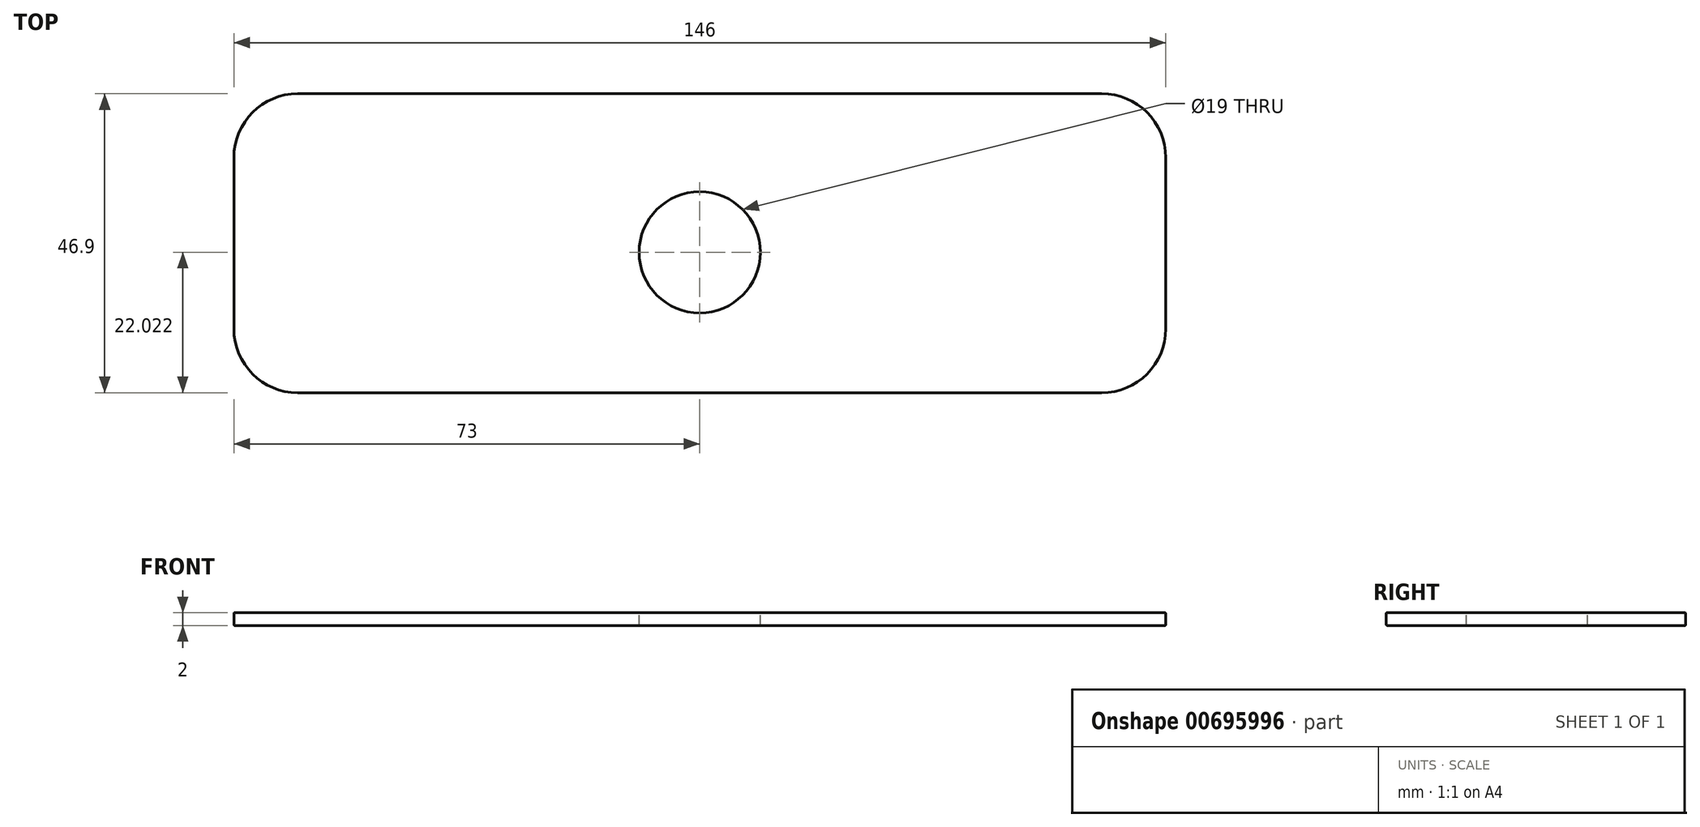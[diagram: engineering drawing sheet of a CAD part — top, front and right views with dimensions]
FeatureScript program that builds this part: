
annotation { "Feature Type Name" : "Feature", "Feature Type Description" : "" }
export const myFeature = defineFeature(function(context is Context, id is Id, definition is map)
    precondition{}
    {
        {
            var Q0;
            Q0=qCreatedBy(makeId("Top.planeOp"),FACE);
            var sketch = newSketch(context, id + "F0", { "sketchPlane" : qUnion([Q0])});
            skLineSegment(sketch, "E0.bottom", {"start": v(73, 23.45) * mm, "end": v(-73, 23.45) * mm});
            skLineSegment(sketch, "E0.top", {"start": v(73, -23.45) * mm, "end": v(-73, -23.45) * mm});
            skLineSegment(sketch, "E0.left", {"start": v(73, 23.45) * mm, "end": v(73, -23.45) * mm});
            skLineSegment(sketch, "E0.right", {"start": v(-73, 23.45) * mm, "end": v(-73, -23.45) * mm});
            skPoint(sketch, "E0.middle", {"position": v(0, 0) * mm});
            skSolve(sketch);
        }
        {
            var Q0;
            Q0=makeQuery(id+"F0.imprint","IMPRINT",FACE,{"disambiguationData":[TD([[makeQuery(id+"F0.imprint","IMPRINT",EDGE,{"derivedFrom":sQuery(id+"F0.wireOp",EDGE,"E0.bottom")}),1.0]])]});
            extrude(context, id + "F1", {"entities" : qUnion([Q0]), "depth" : 2 * mm, "offsetDistance" : 25 * mm});
        }
        {
            var Q0;
            Q0=makeQuery(id+"F1.opExtrude","SWEPT_EDGE",EDGE,{"disambiguationData":[OSD([sQuery(id+"F0.wireOp",EDGE,"E0.top"),sQuery(id+"F0.wireOp",EDGE,"E0.left")])]});
            var Q1;
            Q1=makeQuery(id+"F1.opExtrude","SWEPT_EDGE",EDGE,{"disambiguationData":[OSD([sQuery(id+"F0.wireOp",EDGE,"E0.bottom"),sQuery(id+"F0.wireOp",EDGE,"E0.left")])]});
            var Q2;
            Q2=makeQuery(id+"F1.opExtrude","SWEPT_EDGE",EDGE,{"disambiguationData":[OSD([sQuery(id+"F0.wireOp",EDGE,"E0.top"),sQuery(id+"F0.wireOp",EDGE,"E0.right")])]});
            var Q3;
            Q3=makeQuery(id+"F1.opExtrude","SWEPT_EDGE",EDGE,{"disambiguationData":[OSD([sQuery(id+"F0.wireOp",EDGE,"E0.bottom"),sQuery(id+"F0.wireOp",EDGE,"E0.right")])]});
            fillet(context, id + "F2", {"entities" : qUnion([Q0, Q1, Q2, Q3]), "radius" : 10 * mm, "tangentPropagation" : true, "allowEdgeOverflow" : false});
        }
        {
            var Q0;
            Q0=makeQuery(id+"F1.opExtrude","CAP_FACE",FACE,{"disambiguationData":[OSD([sQuery(id+"F0.wireOp",EDGE,"E0.bottom"),sQuery(id+"F0.wireOp",EDGE,"E0.top"),sQuery(id+"F0.wireOp",EDGE,"E0.left"),sQuery(id+"F0.wireOp",EDGE,"E0.right")])],"isStart":false});
            var sketch = newSketch(context, id + "F3", { "sketchPlane" : qUnion([Q0])});
            skCircle(sketch, "E1", {"center": v(0, -1.43) * mm, "radius": 9.5 * mm});
            skSolve(sketch);
        }
        {
            var Q0;
            Q0=makeQuery(id+"F3.imprint","IMPRINT",FACE,{"disambiguationData":[TD([[makeQuery(id+"F3.imprint","IMPRINT",EDGE,{"derivedFrom":sQuery(id+"F3.wireOp",EDGE,"E1")}),1.0]])]});
            extrude(context, id + "F4", {"entities" : qUnion([Q0]), "operationType" : NewBodyOperationType.REMOVE, "oppositeDirection" : true, "depth" : 25 * mm, "offsetDistance" : 25 * mm});
        }
        {
            var Q0;
            Q0=makeQuery(id+"F1.opExtrude","CAP_FACE",FACE,{"disambiguationData":[OSD([sQuery(id+"F0.wireOp",EDGE,"E0.bottom"),sQuery(id+"F0.wireOp",EDGE,"E0.top"),sQuery(id+"F0.wireOp",EDGE,"E0.left"),sQuery(id+"F0.wireOp",EDGE,"E0.right")])],"isStart":false});
            var Q1;
            Q1=makeQuery(id+"F1.opExtrude","CAP_FACE",FACE,{"disambiguationData":[OSD([sQuery(id+"F0.wireOp",EDGE,"E0.bottom"),sQuery(id+"F0.wireOp",EDGE,"E0.top"),sQuery(id+"F0.wireOp",EDGE,"E0.left"),sQuery(id+"F0.wireOp",EDGE,"E0.right")])],"isStart":true});
            var Q2;
            Q2=makeQuery(id+"F4.boolean.opBoolean","COPY",EDGE,{"derivedFrom":makeQuery(id+"F4.opExtrude","CAP_EDGE",EDGE,{"disambiguationData":[OSD([sQuery(id+"F3.wireOp",EDGE,"E1")])],"isStart":true})});
            var Q3;
            Q3=makeQuery(id+"F4.boolean.opBoolean","INTERSECT",EDGE,{"derivedFrom":[makeQuery(id+"F1.opExtrude","CAP_FACE",FACE,{"disambiguationData":[OSD([sQuery(id+"F0.wireOp",EDGE,"E0.bottom"),sQuery(id+"F0.wireOp",EDGE,"E0.top"),sQuery(id+"F0.wireOp",EDGE,"E0.left"),sQuery(id+"F0.wireOp",EDGE,"E0.right")])],"isStart":true}),makeQuery(id+"F4.opExtrude","SWEPT_FACE",FACE,{"disambiguationData":[OSD([sQuery(id+"F3.wireOp",EDGE,"E1")])]})]});
            fillet(context, id + "F5", {"entities" : qUnion([Q0, Q1, Q2, Q3]), "radius" : .1 * mm, "tangentPropagation" : true, "allowEdgeOverflow" : false});
        }
    });
